annotation { "Feature Type Name" : "Feature", "Feature Type Description" : "" }
export const myFeature = defineFeature(function(context is Context, id is Id, definition is map)
    precondition{}
    {
        {
            var Q0;
            Q0=qCreatedBy(makeId("Front.planeOp"),FACE);
            var sketch = newSketch(context, id + "F0", { "sketchPlane" : qUnion([Q0])});
            skLineSegment(sketch, "E0", {"start": v(0, 0) * mm, "end": v(-4572, 0) * mm});
            skLineSegment(sketch, "E1", {"start": v(0, 0) * mm, "end": v(4572, 0) * mm});
            skLineSegment(sketch, "E2", {"start": v(0, 0) * mm, "end": v(0, 2286) * mm});
            skLineSegment(sketch, "E3", {"start": v(0, 2286) * mm, "end": v(-4572, 0) * mm});
            skLineSegment(sketch, "E4", {"start": v(0, 2286) * mm, "end": v(4572, 0) * mm});
            skLineSegment(sketch, "E5", {"start": v(-4572, 0) * mm, "end": v(-4572, -3352.8) * mm});
            skLineSegment(sketch, "E6", {"start": v(-4572, -3352.8) * mm, "end": v(4572, -3352.8) * mm});
            skLineSegment(sketch, "E7", {"start": v(4572, -3352.8) * mm, "end": v(4572, 0) * mm});
            skLineSegment(sketch, "E8", {"start": v(-4572, -3352.8) * mm, "end": v(-4572, -3962.4) * mm});
            skLineSegment(sketch, "E9", {"start": v(-4572, -3962.4) * mm, "end": v(4572, -3962.4) * mm});
            skLineSegment(sketch, "E10", {"start": v(4572, -3352.8) * mm, "end": v(4572, -3962.4) * mm});
            skLineSegment(sketch, "E11", {"start": v(-2438.4, -3352.8) * mm, "end": v(-2438.4, -1219.2) * mm});
            skLineSegment(sketch, "E12", {"start": v(-2438.4, -1219.2) * mm, "end": v(-3352.8, -1219.2) * mm});
            skLineSegment(sketch, "E13", {"start": v(-3352.8, -1219.2) * mm, "end": v(-3352.8, -3352.8) * mm});
            skLineSegment(sketch, "E14", {"start": v(-2133.6, -3352.8) * mm, "end": v(-2133.6, -914.4) * mm});
            skLineSegment(sketch, "E15", {"start": v(-2133.6, -914.4) * mm, "end": v(-3657.6, -914.4) * mm});
            skLineSegment(sketch, "E16", {"start": v(-3657.6, -914.4) * mm, "end": v(-3657.6, -3352.8) * mm});
            skLineSegment(sketch, "E17.bottom", {"start": v(457.2, -990.6) * mm, "end": v(3200.4, -990.6) * mm});
            skLineSegment(sketch, "E17.top", {"start": v(457.2, -2362.2) * mm, "end": v(3200.4, -2362.2) * mm});
            skLineSegment(sketch, "E17.left", {"start": v(457.2, -990.6) * mm, "end": v(457.2, -2362.2) * mm});
            skLineSegment(sketch, "E17.right", {"start": v(3200.4, -990.6) * mm, "end": v(3200.4, -2362.2) * mm});
            skLineSegment(sketch, "E18.bottom", {"start": v(304.8, -838.2) * mm, "end": v(3352.8, -838.2) * mm});
            skLineSegment(sketch, "E18.top", {"start": v(304.8, -2514.6) * mm, "end": v(3352.8, -2514.6) * mm});
            skLineSegment(sketch, "E18.left", {"start": v(304.8, -838.2) * mm, "end": v(304.8, -2514.6) * mm});
            skLineSegment(sketch, "E18.right", {"start": v(3352.8, -838.2) * mm, "end": v(3352.8, -2514.6) * mm});
            skText(sketch, "E19", { "text": "QUINTEN SCHULTE", "fontName": "OpenSans-Regular.ttf"});
            skLineSegment(sketch, "E20", {"start": v(-4572, 0) * mm, "end": v(-5486.4, 0) * mm});
            skLineSegment(sketch, "E21", {"start": v(-5486.4, 0) * mm, "end": v(7.78, 2747.09) * mm});
            skLineSegment(sketch, "E22", {"start": v(7.78, 2747.09) * mm, "end": v(5486.4, 0) * mm});
            skLineSegment(sketch, "E23", {"start": v(5486.4, 0) * mm, "end": v(4572, 0) * mm});
            skLineSegment(sketch, "E24", {"start": v(4572, -3352.8) * mm, "end": v(9144, -3352.8) * mm});
            skLineSegment(sketch, "E25", {"start": v(9144, -3352.8) * mm, "end": v(9144, -3962.4) * mm});
            skLineSegment(sketch, "E26", {"start": v(9144, -3962.4) * mm, "end": v(4572, -3962.4) * mm});
            skLineSegment(sketch, "E27", {"start": v(9144, -3352.8) * mm, "end": v(9144, -609.6) * mm});
            skLineSegment(sketch, "E28", {"start": v(9144, -609.6) * mm, "end": v(4572, 0) * mm});
            skLineSegment(sketch, "E29", {"start": v(9144, -1219.2) * mm, "end": v(4572, -609.6) * mm});
            skLineSegment(sketch, "E30.bottom", {"start": v(6096, -1143) * mm, "end": v(7315.2, -1143) * mm});
            skLineSegment(sketch, "E30.top", {"start": v(6096, -2514.6) * mm, "end": v(7315.2, -2514.6) * mm});
            skLineSegment(sketch, "E30.left", {"start": v(6096, -1143) * mm, "end": v(6096, -2514.6) * mm});
            skLineSegment(sketch, "E30.right", {"start": v(7315.2, -1143) * mm, "end": v(7315.2, -2514.6) * mm});
            skLineSegment(sketch, "E31.bottom", {"start": v(6248.4, -1295.4) * mm, "end": v(7162.8, -1295.4) * mm});
            skLineSegment(sketch, "E31.top", {"start": v(6248.4, -2362.2) * mm, "end": v(7162.8, -2362.2) * mm});
            skLineSegment(sketch, "E31.left", {"start": v(6248.4, -1295.4) * mm, "end": v(6248.4, -2362.2) * mm});
            skLineSegment(sketch, "E31.right", {"start": v(7162.8, -1295.4) * mm, "end": v(7162.8, -2362.2) * mm});
            const initialGuessF0  = {"E19": [-11.53396, -5.99746, 1, 0, 1.98534]};
            skSetInitialGuess(sketch, initialGuessF0);
            skSolve(sketch);
        }
        {
            var Q0;
            Q0=makeQuery(id+"F0.imprint","IMPRINT",FACE,{"disambiguationData":[TD([[makeQuery(id+"F0.imprint","IMPRINT",EDGE,{"derivedFrom":sQuery(id+"F0.wireOp",EDGE,"E0")}),1.0]])]});
            var Q1;
            Q1=makeQuery(id+"F0.imprint","IMPRINT",FACE,{"disambiguationData":[TD([[makeQuery(id+"F0.imprint","IMPRINT",EDGE,{"derivedFrom":sQuery(id+"F0.wireOp",EDGE,"E17.bottom")}),-1.0]])]});
            var Q2;
            {var subQ0=sQuery(id+"F0.wireOp",EDGE,"E11");Q2=makeQuery(id+"F0.imprint","IMPRINT",FACE,{"disambiguationData":[TD([[makeQuery(id+"F0.imprint","IMPRINT",EDGE,{"derivedFrom":subQ0}),1.0]])]});}
            var Q3;
            Q3=makeQuery(id+"F0.imprint","IMPRINT",FACE,{"disambiguationData":[TD([[makeQuery(id+"F0.imprint","IMPRINT",EDGE,{"derivedFrom":sQuery(id+"F0.wireOp",EDGE,"E31.bottom")}),-1.0]])]});
            var Q4;
            {var subQ1=sQuery(id+"F0.wireOp",EDGE,"E24");Q4=makeQuery(id+"F0.imprint","IMPRINT",FACE,{"disambiguationData":[TD([[makeQuery(id+"F0.imprint","IMPRINT",EDGE,{"derivedFrom":subQ1}),1.0]])]});}
            var Q5;
            Q5=makeQuery(id+"F0.imprint","IMPRINT",FACE,{"disambiguationData":[TD([[makeQuery(id+"F0.imprint","IMPRINT",EDGE,{"derivedFrom":sQuery(id+"F0.wireOp",EDGE,"E1")}),1.0]])]});
            var Q6;
            Q6=makeQuery(id+"F0.imprint","IMPRINT",FACE,{"disambiguationData":[TD([[makeQuery(id+"F0.imprint","IMPRINT",EDGE,{"derivedFrom":sQuery(id+"F0.wireOp",EDGE,"E0")}),-1.0]])]});
            extrude(context, id + "F1", {"entities" : qUnion([Q0, Q1, Q2, Q3, Q4, Q5, Q6]), "endBound" : BoundingType.SYMMETRIC, "depth" : 12192 * mm, "offsetDistance" : 30.48 * mm});
        }
        {
            var Q0;
            {var subQ0=sQuery(id+"F0.wireOp",EDGE,"E11");Q0=makeQuery(id+"F0.imprint","IMPRINT",FACE,{"disambiguationData":[TD([[makeQuery(id+"F0.imprint","IMPRINT",EDGE,{"derivedFrom":subQ0}),-1.0]])]});}
            var Q1;
            Q1=makeQuery(id+"F0.imprint","IMPRINT",FACE,{"disambiguationData":[TD([[makeQuery(id+"F0.imprint","IMPRINT",EDGE,{"derivedFrom":sQuery(id+"F0.wireOp",EDGE,"E17.bottom")}),1.0]])]});
            var Q2;
            Q2=makeQuery(id+"F0.imprint","IMPRINT",FACE,{"disambiguationData":[TD([[makeQuery(id+"F0.imprint","IMPRINT",EDGE,{"derivedFrom":sQuery(id+"F0.wireOp",EDGE,"E30.bottom")}),-1.0]])]});
            extrude(context, id + "F2", {"entities" : qUnion([Q0, Q1, Q2]), "endBound" : BoundingType.SYMMETRIC, "depth" : 12801.6 * mm, "offsetDistance" : 30.48 * mm});
        }
        {
            var Q0;
            {var subQ5=sQuery(id+"F0.wireOp",EDGE,"E8");Q0=makeQuery(id+"F0.imprint","IMPRINT",FACE,{"disambiguationData":[TD([[makeQuery(id+"F0.imprint","IMPRINT",EDGE,{"derivedFrom":subQ5}),1.0]])]});}
            var Q1;
            Q1=makeQuery(id+"F0.imprint","IMPRINT",FACE,{"disambiguationData":[TD([[makeQuery(id+"F0.imprint","IMPRINT",EDGE,{"derivedFrom":sQuery(id+"F0.wireOp",EDGE,"E10")}),1.0]])]});
            var Q2;
            {var subQ0=sQuery(id+"F0.wireOp",EDGE,"E28");Q2=makeQuery(id+"F0.imprint","IMPRINT",FACE,{"disambiguationData":[TD([[makeQuery(id+"F0.imprint","IMPRINT",EDGE,{"derivedFrom":subQ0}),1.0]])]});}
            var Q3;
            Q3=makeQuery(id+"F0.imprint","IMPRINT",FACE,{"disambiguationData":[TD([[makeQuery(id+"F0.imprint","IMPRINT",EDGE,{"derivedFrom":sQuery(id+"F0.wireOp",EDGE,"E3")}),-1.0]])]});
            extrude(context, id + "F3", {"entities" : qUnion([Q0, Q1, Q2, Q3]), "endBound" : BoundingType.SYMMETRIC, "depth" : 14630.4 * mm, "offsetDistance" : 30.48 * mm});
        }
        {
            var Q0;
            Q0=makeQuery(id+"F3.opExtrude","SWEPT_FACE",FACE,{"disambiguationData":[OSD([sQuery(id+"F0.wireOp",EDGE,"E6"),sQuery(id+"F0.wireOp",EDGE,"E24")])]});
            var sketch = newSketch(context, id + "F4", { "sketchPlane" : qUnion([Q0])});
            skText(sketch, "E32", { "text": "quinten schulte", "fontName": "OpenSans-Regular.ttf"});
            const initialGuessF4  = {"E32": [-4.572, -7.0104, 1, 0, 1.36382]};
            skSetInitialGuess(sketch, initialGuessF4);
            skSolve(sketch);
        }
        {
            var Q0;
            Q0 = qSketchRegion(id + "F4", true);
            extrude(context, id + "F5", {"entities" : qUnion([Q0]), "depth" : 304.8 * mm, "offsetDistance" : 30.48 * mm});
        }
    });